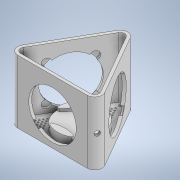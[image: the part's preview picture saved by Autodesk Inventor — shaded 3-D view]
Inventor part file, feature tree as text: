
AUTODESK INVENTOR PART (.ipt)
format: ipt  version: 2022.4 (Build 264492010, 492A)  size: 417,792 bytes
history: native  units: mm
features: sketch x11, extrude x7, pattern_circular x3, plane x2, shell x1, revolve x1, fillet x1, hole x1
ambient origin geometry x8: Origin, YZ Plane, XZ Plane, XY Plane, X Axis, Y Axis, Z Axis, Center Point
bodies: Solid1 (feature_tree)
feature tree (27):
  extrude  "Extrusion1"  Depth=37.0mm
  shell  "Shell1"  Thickness=37.0mm
  sketch  "Sketch16"  dims[d18=212.772423mm]
  extrude  "Extrusion9"  TaperAngle=30.0deg  [1 undecoded]
  sketch  "Sketch4"  dims[d12=30.0deg d13=30.0deg]
  plane  "Work Plane1"
  extrude  "Extrusion6"  TaperAngle=30.0deg  [1 undecoded]
  sketch  "Sketch11"  dims[d16=30.0deg d17=30.0deg]
  extrude  "Extrusion8"  TaperAngle=30.0deg  [1 undecoded]
  pattern_circular  "Circular Pattern3"  Angle=120.0deg  [1 undecoded]
  pattern_circular  "Circular Pattern4"  Angle=120.0deg  [1 undecoded]
  extrude  "Extrusion10"  TaperAngle=45.0deg  [1 undecoded]
  sketch  "Sketch20"  dims[d21=0.0mm]
  revolve  "Revolution4"  [1 undecoded]
  fillet  "Fillet1"  Radius=11.0mm
  plane  "Work Plane2"
  extrude  "Extrusion12"  Depth=4.0mm TaperAngle=360.0deg
  extrude  "Extrusion13"  Depth=4.0mm TaperAngle=0.0deg
  hole  "Hole3"  [1 undecoded]
  pattern_circular  "Circular Pattern7"  Count=3 Angle=360.0deg
  sketch  "Sketch1"  dims[d4=37.0mm d5=37.0mm d6=37.0mm]
  sketch  "Sketch8"  dims[d14=30.0deg d15=30.0deg]
  sketch  "Sketch19"  dims[d19=0.0mm]
  sketch  "Sketch21"  dims[d22=85.0mm d23=0.0mm]
  sketch  "Sketch24"  dims[d24=4.0mm]
  sketch  "Sketch25"  dims[d30=74.0mm]
  sketch  "Sketch26"  dims[d36=120.0deg d37=120.0deg d38=120.0deg d39=45.0deg d40=24.0mm d41=11.0mm d42=40.0mm d44=360.0deg d61=2.0mm d62=0.0mm d85=3.5mm d86=0.0mm d87=30.0mm d88=360.0deg d113=64.0mm d114=5.0mm d115=0.0mm d116=30.0mm d117=360.0deg d130=64.08588mm d131=60.0mm d132=10.0mm d133=10.0mm d140=64.856mm d141=89.0mm d142=89.0mm d143=64.856mm d144=89.0mm d145=64.856mm d146=4.0mm d147=0.0mm d148=55.5mm d149=38.75mm d150=38.75mm d151=30.0deg d153=2.0mm d193=42.5mm d194=42.5mm d195=85.0mm d196=6.5mm d197=0.0mm d198=0.0mm d199=6.25mm d200=0.0mm d201=60.0deg d202=60.0deg d203=9.0mm d204=9.0mm d205=2.0mm d206=2.0mm d207=2.0mm d208=2.0mm d209=2.0mm d210=2.0mm d211=2.0mm d212=2.0mm d213=2.0mm d214=2.0mm d215=2.0mm d216=4.0mm d217=4.0mm d218=4.0mm d219=4.0mm d220=4.0mm d221=4.0mm d222=4.0mm d223=4.0mm d224=4.0mm d225=2.0mm d227=4.0mm d228=2.0mm d229=2.0mm d230=2.0mm d231=0.0mm d232=0.0mm d233=3.7mm d234=6.0mm d235=4.0mm d236=2.0mm d237=90.0deg d238=8.0mm d239=20.594885mm d240=30.0mm d241=360.0deg]
note: 8 required parameter values undecoded (feature->parameter linkage not recoverable at this tier; creation-order binding heuristic only, values carry confidence <= 0.55)